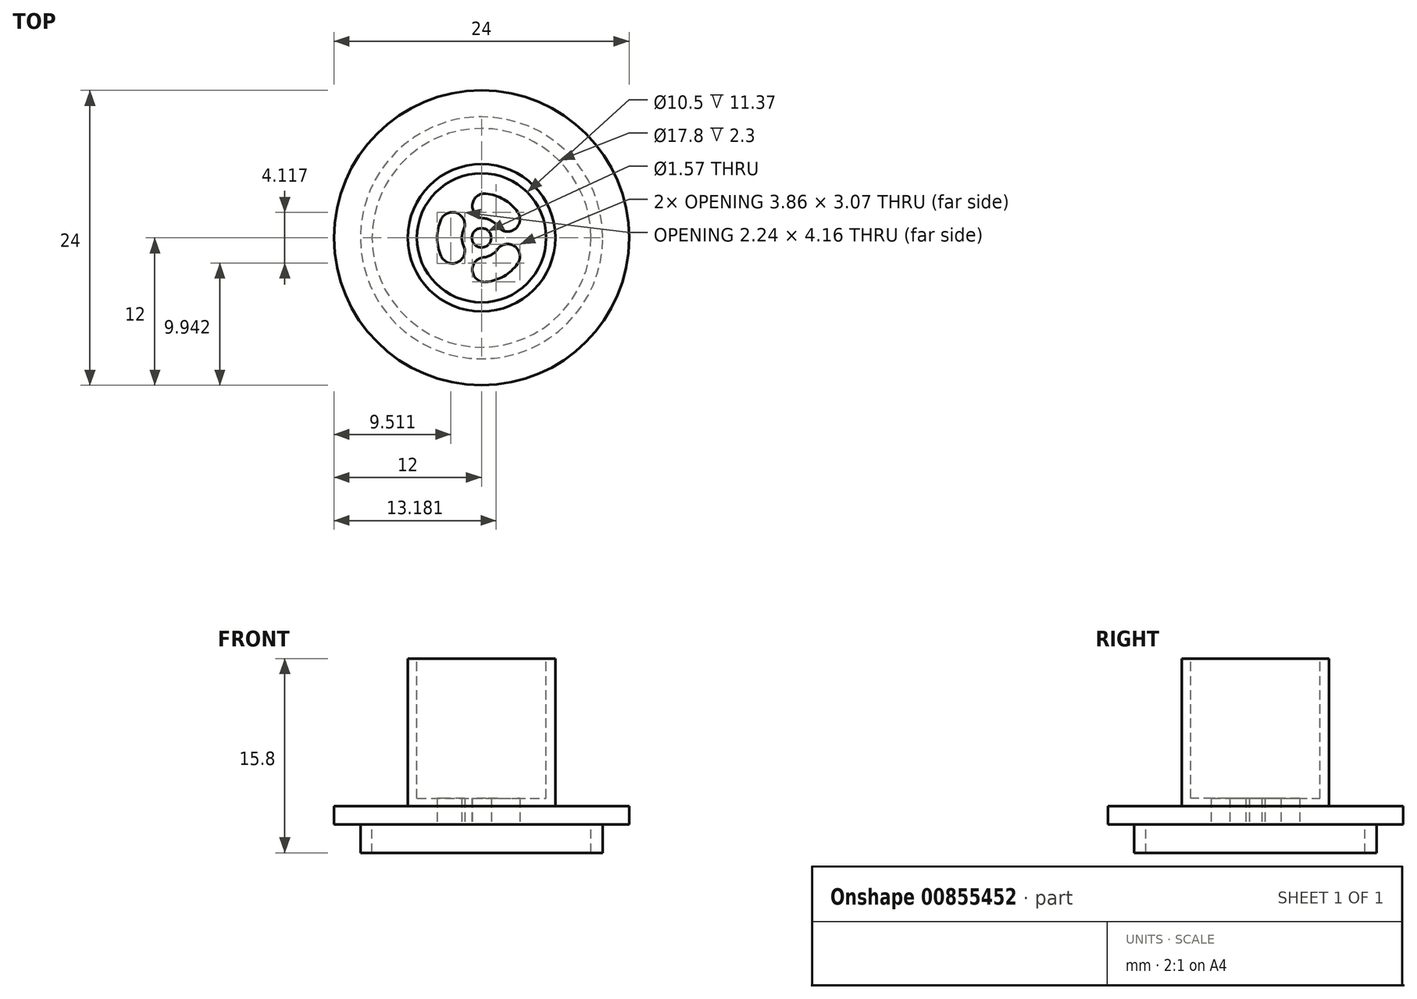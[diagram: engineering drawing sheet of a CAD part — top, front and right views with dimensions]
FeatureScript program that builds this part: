
annotation { "Feature Type Name" : "Feature", "Feature Type Description" : "" }
export const myFeature = defineFeature(function(context is Context, id is Id, definition is map)
    precondition{}
    {
        {
            var Q0;
            Q0=qCreatedBy(makeId("Right.planeOp"),FACE);
            var sketch = newSketch(context, id + "F0", { "sketchPlane" : qUnion([Q0])});
            skLineSegment(sketch, "E0", {"start": v(0, 0) * mm, "end": v(8.9, 0) * mm});
            skLineSegment(sketch, "E1", {"start": v(8.9, 0) * mm, "end": v(8.9, -2.3) * mm});
            skLineSegment(sketch, "E2", {"start": v(8.9, -2.3) * mm, "end": v(9.85, -2.3) * mm});
            skLineSegment(sketch, "E3", {"start": v(9.85, -2.3) * mm, "end": v(9.85, 0) * mm});
            skLineSegment(sketch, "E4", {"start": v(9.85, 0) * mm, "end": v(12, 0) * mm});
            skLineSegment(sketch, "E5", {"start": v(12, 0) * mm, "end": v(12, 1.5) * mm});
            skLineSegment(sketch, "E6", {"start": v(12, 1.5) * mm, "end": v(6, 1.5) * mm});
            skLineSegment(sketch, "E7", {"start": v(6, 1.5) * mm, "end": v(6, 13.5) * mm});
            skLineSegment(sketch, "E8", {"start": v(6, 13.5) * mm, "end": v(0, 13.5) * mm});
            skLineSegment(sketch, "E9", {"start": v(0, 13.5) * mm, "end": v(0, 0) * mm});
            skSolve(sketch);
        }
        {
            var Q0;
            Q0 = qSketchRegion(id + "F0", true);
            var Q1;
            Q1=sQuery(id+"F0.wireOp",EDGE,"E9");
            revolve(context, id + "F1", {"surfaceOperationType" : NewSurfaceOperationType.NEW, "entities" : qUnion([Q0]), "axis" : qUnion([Q1]), "revolveType" : RevolveType.FULL});
        }
        {
            var Q0;
            Q0=makeQuery(id+"F1.opRevolve","SWEPT_FACE",FACE,{"disambiguationData":[OSD([sQuery(id+"F0.wireOp",EDGE,"E8")])]});
            var sketch = newSketch(context, id + "F2", { "sketchPlane" : qUnion([Q0])});
            skCircle(sketch, "E10", {"center": v(0, 0) * mm, "radius": 5.25 * mm});
            skSolve(sketch);
        }
        {
            var Q0;
            Q0 = qSketchRegion(id + "F2", true);
            extrude(context, id + "F3", {"entities" : qUnion([Q0]), "operationType" : NewBodyOperationType.REMOVE, "endBound" : BoundingType.THROUGH_ALL, "oppositeDirection" : true, "depth" : 25 * mm, "offsetDistance" : 25 * mm});
        }
        {
            var Q0;
            Q0=makeQuery(id+"F1.opRevolve","SWEPT_FACE",FACE,{"disambiguationData":[OSD([sQuery(id+"F0.wireOp",EDGE,"E0")])]});
            var sketch = newSketch(context, id + "F4", { "sketchPlane" : qUnion([Q0])});
            skCircle(sketch, "E11.0", {"center": v(0, 0) * mm, "radius": 5.25 * mm});
            skArc(sketch, "E12", {"start": v(0.16, -1.6) * mm, "mid": v(0.8, -1.39) * mm, "end": v(1.3, -0.93) * mm});
            skArc(sketch, "E13", {"start": v(0.35, -3.6) * mm, "mid": v(1.8, -3.13) * mm, "end": v(2.94, -2.1) * mm});
            skCircle(sketch, "E14", {"center": v(0, 0) * mm, "radius": 0.79 * mm});
            skArc(sketch, "E15", {"start": v(2.94, -2.1) * mm, "mid": v(2.7, -0.7) * mm, "end": v(1.3, -0.93) * mm});
            skArc(sketch, "E16.MirrorC", {"start": v(2.94, 2.1) * mm, "mid": v(2.7, 0.7) * mm, "end": v(1.3, 0.93) * mm});
            skArc(sketch, "E17.1.0", {"start": v(0.35, 3.6) * mm, "mid": v(-0.75, 2.7) * mm, "end": v(0.16, 1.6) * mm});
            skArc(sketch, "E17.1.1", {"start": v(-3.29, 1.5) * mm, "mid": v(-1.96, 2) * mm, "end": v(-1.46, 0.66) * mm});
            skArc(sketch, "E17.2.0", {"start": v(-3.29, -1.5) * mm, "mid": v(-1.96, -2) * mm, "end": v(-1.46, -0.66) * mm});
            skArc(sketch, "E17.2.1", {"start": v(0.35, -3.6) * mm, "mid": v(-0.75, -2.7) * mm, "end": v(0.16, -1.6) * mm});
            skArc(sketch, "E18.trimOffspring", {"start": v(1.3, 0.93) * mm, "mid": v(0.8, 1.39) * mm, "end": v(0.16, 1.6) * mm});
            skArc(sketch, "E19.trimOffspring", {"start": v(2.94, 2.1) * mm, "mid": v(1.8, 3.13) * mm, "end": v(0.35, 3.6) * mm});
            skArc(sketch, "E20.trimOffspring", {"start": v(-1.46, 0.66) * mm, "mid": v(-1.6, 0) * mm, "end": v(-1.46, -0.66) * mm});
            skArc(sketch, "E21.trimOffspring", {"start": v(-3.29, 1.5) * mm, "mid": v(-3.6, 0) * mm, "end": v(-3.29, -1.5) * mm});
            skSolve(sketch);
        }
        {
            var Q0;
            Q0 = qSketchRegion(id + "F4", true);
            var Q1;
            Q1 = qConstructionFilter(qBodyType(qCreatedBy(id + "F4" ,EDGE), BodyType.WIRE), ConstructionObject.NO);
            extrude(context, id + "F5", {"entities" : qUnion([Q0]), "operationType" : NewBodyOperationType.ADD, "surfaceEntities" : qUnion([Q1]), "oppositeDirection" : true, "depth" : 2.13 * mm, "offsetDistance" : 25 * mm});
        }
    });
